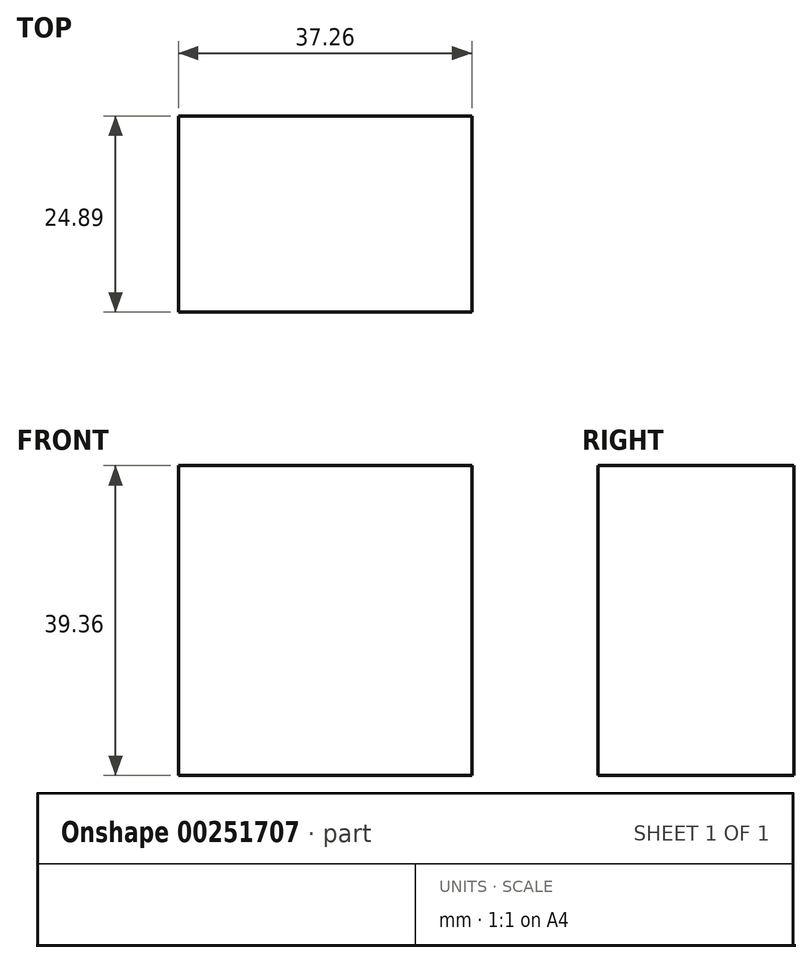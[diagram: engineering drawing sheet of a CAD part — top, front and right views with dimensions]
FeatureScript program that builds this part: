
annotation { "Feature Type Name" : "Feature", "Feature Type Description" : "" }
export const myFeature = defineFeature(function(context is Context, id is Id, definition is map)
    precondition{}
    {
        {
            var Q0;
            Q0=qCreatedBy(makeId("Front.planeOp"),FACE);
            var sketch = newSketch(context, id + "F0", { "sketchPlane" : qUnion([Q0])});
            skLineSegment(sketch, "E0.bottom", {"start": v(-118.38, 49.58) * mm, "end": v(-81.12, 49.58) * mm});
            skLineSegment(sketch, "E0.top", {"start": v(-118.38, 10.22) * mm, "end": v(-81.12, 10.22) * mm});
            skLineSegment(sketch, "E0.left", {"start": v(-118.38, 49.58) * mm, "end": v(-118.38, 10.22) * mm});
            skLineSegment(sketch, "E0.right", {"start": v(-81.12, 49.58) * mm, "end": v(-81.12, 10.22) * mm});
            skSolve(sketch);
        }
        {
            var Q0;
            Q0 = qSketchRegion(id + "F0", true);
            extrude(context, id + "F1", {"entities" : qUnion([Q0]), "depth" : 24.9 * mm});
        }
    });
